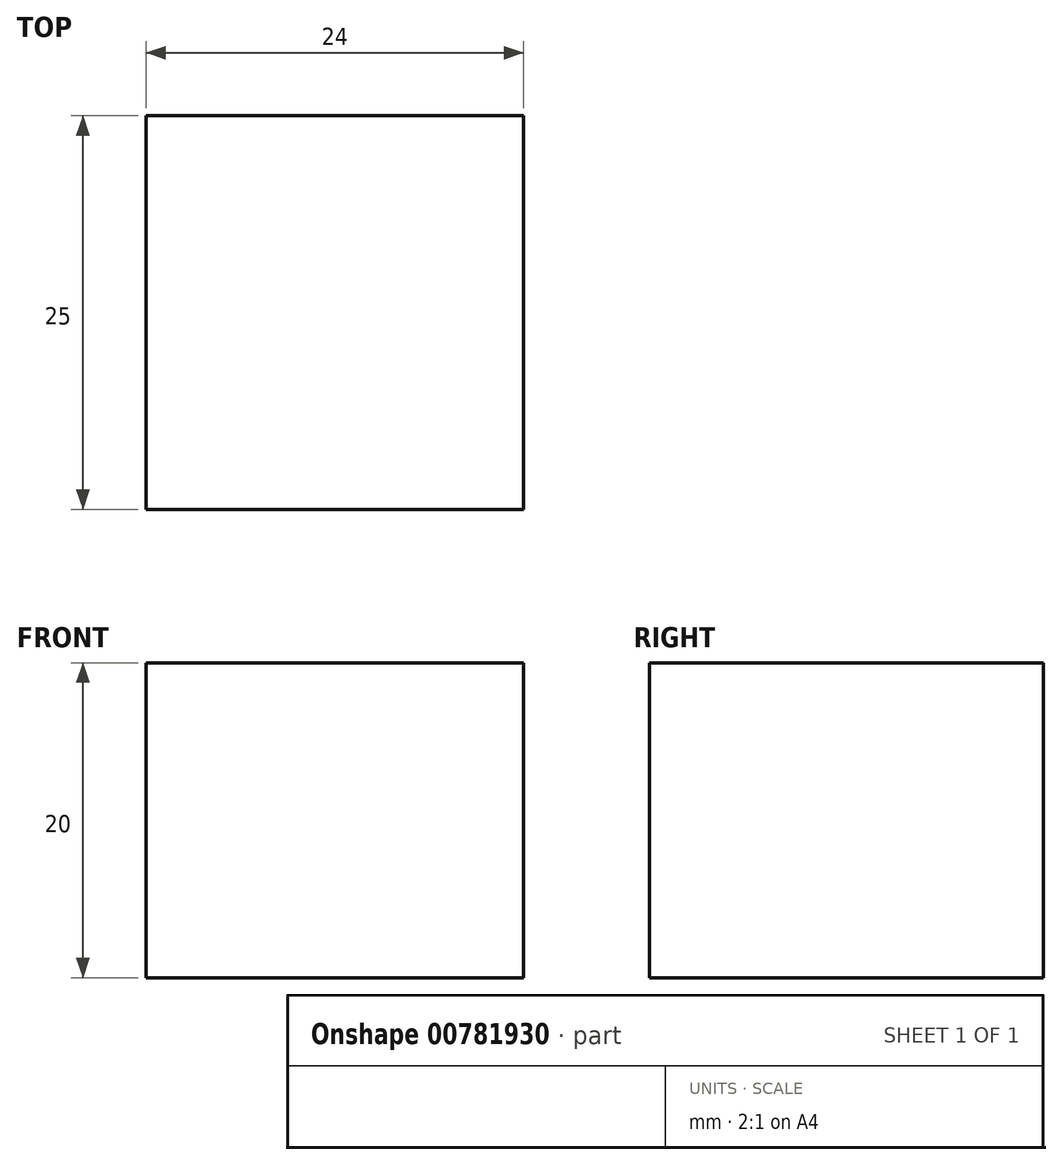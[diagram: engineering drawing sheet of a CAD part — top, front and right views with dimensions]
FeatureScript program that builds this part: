
annotation { "Feature Type Name" : "Feature", "Feature Type Description" : "" }
export const myFeature = defineFeature(function(context is Context, id is Id, definition is map)
    precondition{}
    {
        {
            var Q0;
            Q0=qCreatedBy(makeId("Front.planeOp"),FACE);
            var sketch = newSketch(context, id + "F0", { "sketchPlane" : qUnion([Q0])});
            skLineSegment(sketch, "E0.bottom", {"start": v(11.71, 7.54) * mm, "end": v(-13.29, 7.54) * mm});
            skLineSegment(sketch, "E0.top", {"start": v(11.71, -12.46) * mm, "end": v(-68.29, -12.46) * mm});
            skLineSegment(sketch, "E0.left", {"start": v(11.71, 7.54) * mm, "end": v(11.71, -12.46) * mm});
            skLineSegment(sketch, "E0.right", {"start": v(-12.29, 12.54) * mm, "end": v(-12.29, -12.46) * mm});
            skSolve(sketch);
        }
        {
            var Q0;
            Q0=qSketchRegion(id+"F0",true);
            extrude(context, id + "F1", {"entities" : qUnion([Q0]), "endBound" : BoundingType.SYMMETRIC, "depth" : 25 * mm, "offsetDistance" : 25 * mm});
        }
    });
